# Revit family: VLGFP1502-xxxSI8xxAxxxx
name_source: partatom
category: Leuchten
revit_build: Autodesk Revit 2017 (Build: 20160225_1515(x64)
units: mm (PartAtom-declared; Revit-internal decimal feet)

## family parameters
Basisbauteil = Fläche
Beim Laden mit Abzugskörper schneiden = Nein
Bemaßung runder Anschluss = Durchmesser verwenden
Gemeinsam genutzt = Nein
Lichtquelle = Ja
OmniClass-Nummer = 23.80.70.11
OmniClass-Titel = Luminaries for Internal Lighting
Raumberechnungspunkt = Nein
Teiletyp = Normal

## types (12) — shared parameters
Baugruppenkennzeichen = D5020200
Datei für fotometrisches Netz = VLGFP1502-5NDWS840A1400.IES
Emissionsform beim Rendern sichtbar = Nein
Farbfilter = 16777215
Farbtemperaturverschiebung bei Dämpfen der Lampe = <Keine Auswahl>
Hersteller = RIDI Leuchten GmbH
Lampe = LED
Neigungswinkel = 90.00°
Scheinlast = 100 VA
URL = www.ridi.de
Von Breite des Rechtecks ausssenden = 1469 mm  [stored 4.81955 ft]
Von Länge des Rechtecks aussenden = 63 mm  [stored 0.206693 ft]
brand = RIDI
conformity mark = CE
electrical safety class = 1
height = 66 mm  [stored 0.216535 ft]
ingress protection (IP) code = IP54
length = 1500 mm  [stored 4.92126 ft]
nominal frequency = 50-60Hz
nominal voltage = 230
rated input power = 100
voltage type (AC, DC, UC) = AC
weight = 2.1 kg
width = 67 mm
zero-valued in all types: Vorgabe-Ansicht

## per-type parameters (varying)
| type | Modell |
| VLGFP1502-5NDSI830A1300 | 1551037SI |
| VLGFP1502-7DASI830A1300 | 1561037SI |
| VLGFP1502-5NDSI830A1400-RF | 1551131SI |
| VLGFP1502-5NDSI840A1400 | 1551019SI |
| VLGFP1502-7DASI840A1400 | 1561019SI |
| VLGFP1502-5NDSI840A1400-RF | 1551132SI |
| VLGFP1502-5NDSI850A1400 | 1551051SI |
| VLGFP1502-7DASI850A1400 | 1561051SI |
| VLGFP1502-5NDSI850A1500-RF | 1551133SI |
| VLGFP1502-5NDSI865A1400 | 1551064SI |
| VLGFP1502-7DASI865A1400 | 1561064SI |
| VLGFP1502-5NDSI865A1400-RF | 1551134SI |

note: column(s) folded — value = type name in every type: product name

note: [stored X ft] marks values corroborated as IEEE doubles in the binary element streams (Revit-internal decimal feet)
